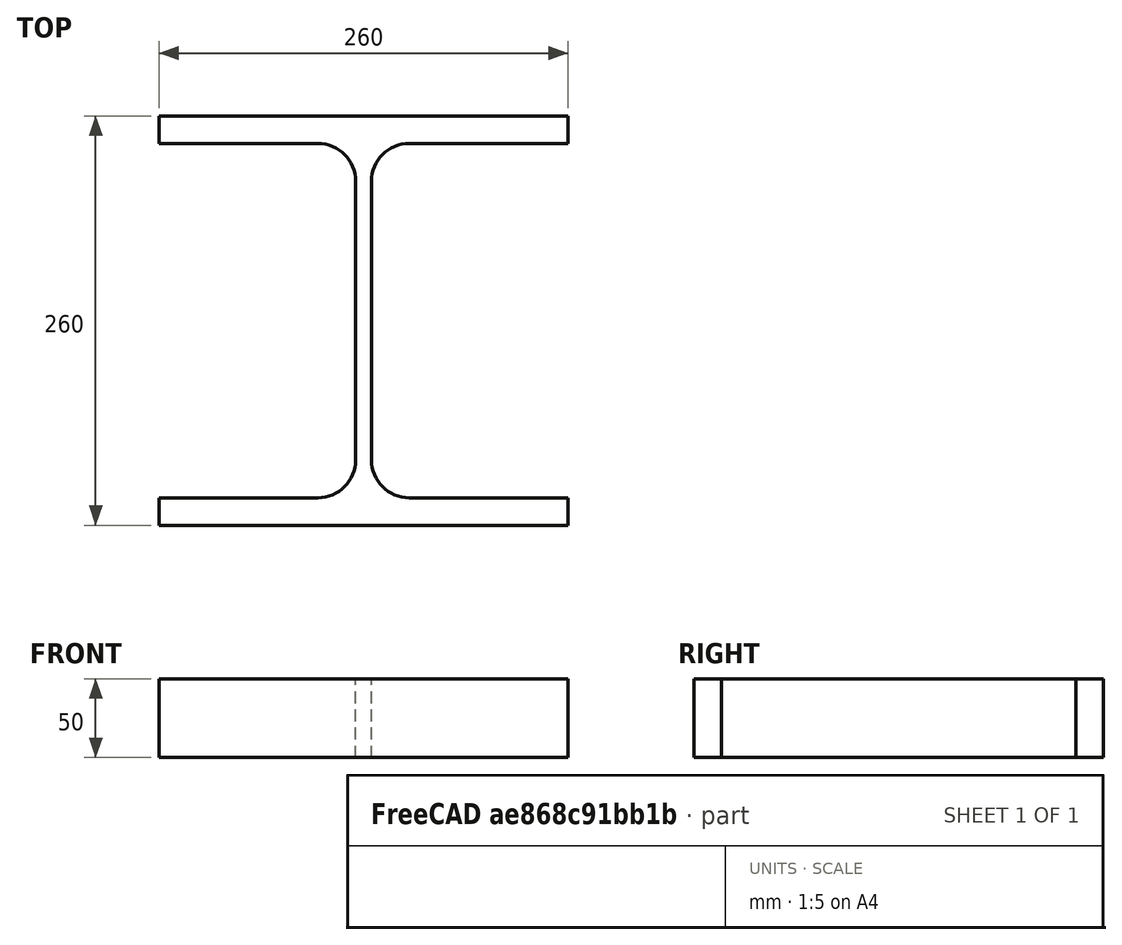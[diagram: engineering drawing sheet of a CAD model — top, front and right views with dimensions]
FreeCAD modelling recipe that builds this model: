
FCSTD DOCUMENT  (FreeCAD 0.15R4671 (Git))
Label: HE-B-Profile 260 DIN1025-2 S235JR
License: All rights reserved
LicenseURL: http://en.wikipedia.org/wiki/All_rights_reserved
objects: Sketcher::SketchObject×1, Part::Extrusion×1
note: 2 computed .brp shape members not serialized (recipe doc carries the construction recipe); baked Part::Feature solids carry a one-line shape summary decoded from their .brp

FEATURE [Sketcher::SketchObject] Sketch
  sketch-geometry (16):
    g0: LineSegment StartX=5 StartY=-88.5 StartZ=0 EndX=5 EndY=88.5 EndZ=0
    g1: LineSegment StartX=29 StartY=112.5 StartZ=0 EndX=130 EndY=112.5 EndZ=0
    g2: LineSegment StartX=130 StartY=112.5 StartZ=0 EndX=130 EndY=130 EndZ=0
    g3: LineSegment StartX=130 StartY=130 StartZ=0 EndX=-130 EndY=130 EndZ=0
    g4: LineSegment StartX=-130 StartY=130 StartZ=0 EndX=-130 EndY=112.5 EndZ=0
    g5: LineSegment StartX=-130 StartY=112.5 StartZ=0 EndX=-29 EndY=112.5 EndZ=0
    g6: LineSegment StartX=-5 StartY=88.5 StartZ=0 EndX=-5 EndY=-88.5 EndZ=0
    g7: LineSegment StartX=-29 StartY=-112.5 StartZ=0 EndX=-130 EndY=-112.5 EndZ=0
    g8: LineSegment StartX=-130 StartY=-112.5 StartZ=0 EndX=-130 EndY=-130 EndZ=0
    g9: LineSegment StartX=-130 StartY=-130 StartZ=0 EndX=130 EndY=-130 EndZ=0
    g10: LineSegment StartX=130 StartY=-130 StartZ=0 EndX=130 EndY=-112.5 EndZ=0
    g11: LineSegment StartX=130 StartY=-112.5 StartZ=0 EndX=29 EndY=-112.5 EndZ=0
    g12: ArcOfCircle CenterX=29 CenterY=88.5 CenterZ=0 NormalX=0 NormalY=0 NormalZ=1 Radius=24 StartAngle=1.5708 EndAngle=3.14159
    g13: ArcOfCircle CenterX=29 CenterY=-88.5 CenterZ=0 NormalX=0 NormalY=0 NormalZ=1 Radius=24 StartAngle=3.14159 EndAngle=4.71239
    g14: ArcOfCircle CenterX=-29 CenterY=88.5 CenterZ=0 NormalX=0 NormalY=0 NormalZ=1 Radius=24 StartAngle=0 EndAngle=1.5708
    g15: ArcOfCircle CenterX=-29 CenterY=-88.5 CenterZ=0 NormalX=0 NormalY=0 NormalZ=1 Radius=24 StartAngle=4.71239 EndAngle=6.28319
  constraints (42):
    c: Vertical(g0)
    c: Coincident(g2,g1)
    c: Vertical(g2)
    c: Coincident(g3,g2)
    c: Coincident(g4,g3)
    c: Vertical(g4)
    c: Coincident(g5,g4)
    c: Horizontal(g5)
    c: Vertical(g6)
    c: Horizontal(g7)
    c: Coincident(g8,g7)
    c: Vertical(g8)
    c: Coincident(g9,g8)
    c: Horizontal(g9)
    c: Coincident(g10,g9)
    c: Vertical(g10)
    c: Coincident(g11,g10)
    c: Horizontal(g11)
    c: Tangent(g1,g12) = 1.5708
    c: Tangent(g0,g12) = 1.5708
    c: Tangent(g0,g13) = 1.5708
    c: Tangent(g11,g13) = 1.5708
    c: Tangent(g5,g14) = 1.5708
    c: Tangent(g6,g14) = 1.5708
    c: Tangent(g6,g15) = 1.5708
    c: Tangent(g7,g15) = 1.5708
    c: Equal(g3,g9)
    c: Equal(g2,g4)
    c: Equal(g4,g8)
    c: Equal(g8,g10)
    c: Equal(g12,g14)
    c: Equal(g14,g15)
    c: Equal(g15,g13)
    c: Symmetric(g2,g3,g-2)
    c: Symmetric(g9,g8,g-2)
    c: Symmetric(g0,g6,g-2)
    c: Symmetric(g2,g9,g-1)
    c: DistanceY(g2,g9) = -260
    c: DistanceX(g3) = -260
    c: DistanceX(g0,g6) = -10
    c: DistanceY(g2) = 17.5
    c: Radius(g12) = 24
FEATURE [Part::Extrusion] Extrude  label="HE-B-Profile 260 DIN1025-2 S235JR"
  Base = -> Sketch
  Dir = (0,0,50)
  Solid = true
